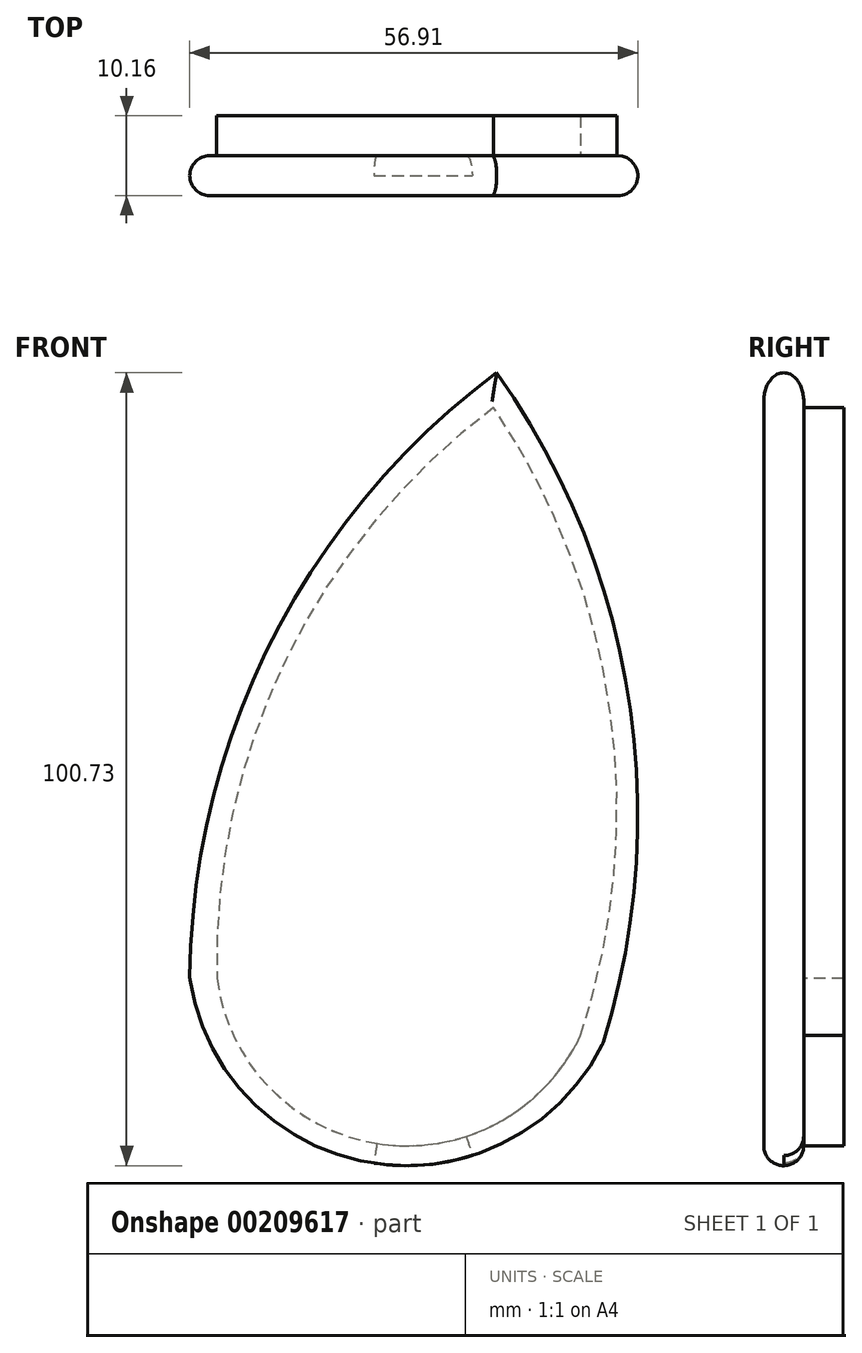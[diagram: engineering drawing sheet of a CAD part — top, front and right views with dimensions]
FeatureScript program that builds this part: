
annotation { "Feature Type Name" : "Feature", "Feature Type Description" : "" }
export const myFeature = defineFeature(function(context is Context, id is Id, definition is map)
    precondition{}
    {
        {
            var Q0;
            Q0=qCreatedBy(makeId("Front.planeOp"),FACE);
            var sketch = newSketch(context, id + "F0", { "sketchPlane" : qUnion([Q0])});
            skArc(sketch, "E0", {"start": v(-25.27, 59.3) * mm, "mid": v(-53.78, 25.4) * mm, "end": v(-64.25, -17.64) * mm});
            skArc(sketch, "E1.MirrorCS", {"start": v(-25.27, 59.3) * mm, "mid": v(-8.53, 18.29) * mm, "end": v(-11.77, -25.9) * mm});
            skArc(sketch, "E2", {"start": v(-64.25, -17.64) * mm, "mid": v(-41.05, -41.1) * mm, "end": v(-11.77, -25.9) * mm});
            skSolve(sketch);
        }
        {
            var Q0;
            Q0=makeQuery(id+"F0.imprint","IMPRINT",FACE,{"disambiguationData":[TD([[makeQuery(id+"F0.imprint","IMPRINT",EDGE,{"derivedFrom":sQuery(id+"F0.wireOp",EDGE,"E0")}),1.0]])]});
            extrude(context, id + "F1", {"entities" : qUnion([Q0]), "depth" : 5.08 * mm});
        }
        {
            var Q0;
            Q0=makeQuery(id+"F1.opExtrude","CAP_FACE",FACE,{"disambiguationData":[OSD([sQuery(id+"F0.wireOp",EDGE,"E0"),sQuery(id+"F0.wireOp",EDGE,"E1.MirrorCS"),sQuery(id+"F0.wireOp",EDGE,"E2")])],"isStart":true});
            var sketch = newSketch(context, id + "F2", { "sketchPlane" : qUnion([Q0])});
            skArc(sketch, "E3", {"start": v(25.64, 54.88) * mm, "mid": v(10.85, 16.29) * mm, "end": v(14.6, -24.86) * mm});
            skArc(sketch, "E4", {"start": v(60.8, -17.64) * mm, "mid": v(52.02, 22.88) * mm, "end": v(25.64, 54.88) * mm});
            skArc(sketch, "E5", {"start": v(14.6, -24.86) * mm, "mid": v(40.41, -38.62) * mm, "end": v(60.8, -17.64) * mm});
            skSolve(sketch);
        }
        {
            var Q0;
            Q0=makeQuery(id+"F2.imprint","IMPRINT",FACE,{"disambiguationData":[TD([[makeQuery(id+"F2.imprint","IMPRINT",EDGE,{"derivedFrom":sQuery(id+"F2.wireOp",EDGE,"E3")}),1.0]])]});
            extrude(context, id + "F3", {"entities" : qUnion([Q0]), "operationType" : NewBodyOperationType.ADD, "depth" : 5.08 * mm});
        }
        {
            var Q0;
            Q0=makeQuery(id+"F1.opExtrude","CAP_FACE",FACE,{"disambiguationData":[OSD([sQuery(id+"F0.wireOp",EDGE,"E0"),sQuery(id+"F0.wireOp",EDGE,"E1.MirrorCS"),sQuery(id+"F0.wireOp",EDGE,"E2")])],"isStart":false});
            var Q1;
            Q1=makeQuery(id+"F1.opExtrude","CAP_EDGE",EDGE,{"disambiguationData":[OSD([sQuery(id+"F0.wireOp",EDGE,"E0")])],"isStart":false});
            var Q2;
            Q2=makeQuery(id+"F1.opExtrude","CAP_EDGE",EDGE,{"disambiguationData":[OSD([sQuery(id+"F0.wireOp",EDGE,"E0")])],"isStart":true});
            var Q3;
            Q3=makeQuery(id+"F1.opExtrude","SWEPT_FACE",FACE,{"disambiguationData":[OSD([sQuery(id+"F0.wireOp",EDGE,"E2")])]});
            var Q4;
            Q4=makeQuery(id+"F1.opExtrude","CAP_EDGE",EDGE,{"disambiguationData":[OSD([sQuery(id+"F0.wireOp",EDGE,"E1.MirrorCS")])],"isStart":true});
            fillet(context, id + "F4", {"entities" : qUnion([Q0, Q1, Q2, Q3, Q4]), "radius" : 2.54 * mm, "tangentPropagation" : true, "allowEdgeOverflow" : false});
        }
    });
